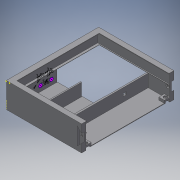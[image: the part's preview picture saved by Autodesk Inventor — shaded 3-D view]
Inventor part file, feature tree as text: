
AUTODESK INVENTOR PART (.ipt)
format: ipt  version: 2016 SP2 (Build 200236200, 236)  size: 1,028,608 bytes
history: native  units: mm
features: sketch x29, extrude x23, chamfer x14, projected_geometry x10, thread x2, revolve x2, other x2
ambient origin geometry x8: Origin, YZ Plane, XZ Plane, XY Plane, X Axis, Y Axis, Z Axis, Center Point
bodies: Volumenkörper1 (feature_tree), Volumenkörper4 (feature_tree), Volumenkörper5 (feature_tree)
feature tree (82):
  extrude  "Extrusion1"  Depth=9.0mm
  extrude  "Extrusion2"  Depth=10.0mm
  extrude  "Extrusion3"  Depth=1.0mm TaperAngle=0.0deg
  extrude  "Extrusion4"  Depth=1.5mm
  extrude  "Extrusion5"  Depth=17.0mm TaperAngle=0.0deg
  sketch  "Skizze6"  dims[d16=3.0mm d17=0.0mm d24=43.5mm]
  chamfer  "Fase2"  Distance=2.0mm
  chamfer  "Fase3"  Distance=23.0mm
  extrude  "Extrusion7"  Depth=43.5mm
  extrude  "Extrusion8"  Depth=2.0mm
  extrude  "Extrusion9"  Depth=1.5mm TaperAngle=45.0deg
  extrude  "Extrusion10"  Depth=78.5mm TaperAngle=0.0deg
  extrude  "Extrusion11"  Depth=82.5mm TaperAngle=0.0deg
  extrude  "Extrusion12"  Depth=2.0mm
  extrude  "Extrusion13"  Depth=1.0mm
  extrude  "Extrusion14"  Depth=2.0mm
  chamfer  "Fase4"  Distance=89.5mm
  chamfer  "Fase5"  Distance=4.5mm
  chamfer  "Fase6"  Distance=4.5mm
  chamfer  "Fase7"  Distance=2.0mm
  chamfer  "Fase9"  Distance=2.0mm
  chamfer  "Fase20"  Distance=2.0mm
  extrude  "Extrusion15"  Depth=2.0mm
  extrude  "Extrusion16"  Depth=5.0mm
  extrude  "Extrusion17"  Depth=5.0mm
  extrude  "Extrusion18"  Depth=40.0mm TaperAngle=0.0deg
  chamfer  "Fase14"  Distance=4.5mm
  chamfer  "Fase15"  Distance=18.0mm
  chamfer  "Fase16"  Distance=2.0mm
  chamfer  "Fase17"  Distance=2.0mm
  chamfer  "Fase18"  Distance=2.0mm
  chamfer  "Fase19"  Distance=2.0mm
  extrude  "Extrusion20"  Depth=10.0mm
  extrude  "Extrusion21"  Depth=10.0mm
  extrude  "Extrusion22"  Depth=10.0mm
  extrude  "Extrusion23"  Depth=10.0mm
  extrude  "Extrusion24"  Depth=10.0mm TaperAngle=0.0deg
  sketch  "Skizze26"  dims[d66=3.5mm d67=4.5mm d68=0.0mm]
  sketch  "Skizze27"  dims[d69=5.6mm d70=2.0mm d71=0.0mm d72=2.0mm d73=2.0mm d74=0.872665mm d75=2.0mm d76=2.0mm d77=0.872665mm]
  extrude  "Extrusion27"  Depth=10.0mm
  thread  "Gewinde3"  [1 undecoded]
  thread  "Gewinde4"  [1 undecoded]
  revolve  "Umdrehung3"
  other  "Spirale3"
  revolve  "Umdrehung4"
  other  "Spirale4"
  sketch  "Skizze1"  dims[d0=9.0mm d1=9.0mm]
  sketch  "Skizze2"  dims[d2=150.5mm d3=10.0mm]
  sketch  "Skizze3"  dims[d4=137.4mm d5=1.0mm d6=0.0mm]
  projected_geometry  "Projizierte Kontur1"
  sketch  "Skizze4"  dims[d7=1.5mm d8=1.5mm]
  projected_geometry  "Projizierte Kontur2"
  projected_geometry  "Projizierte Kontur3"
  projected_geometry  "Projizierte Kontur4"
  sketch  "Skizze5"  dims[d9=4.0mm d10=17.0mm d11=0.0mm d12=2.0mm d13=0.0mm d14=23.0mm d15=0.0mm]
  sketch  "Skizze7"  dims[d25=43.5mm d26=2.0mm]
  sketch  "Skizze8"  dims[d27=3.0mm d33=1.5mm d34=2.0mm d35=45.0deg]
  sketch  "Skizze9"  dims[d36=1.5mm d37=2.0mm d38=45.0deg d39=78.5mm d40=0.0mm]
  sketch  "Skizze10"  dims[d42=23.0mm d43=0.0mm d44=82.5mm d45=0.0mm]
  sketch  "Skizze11"  dims[d46=2.5mm d47=2.0mm]
  sketch  "Skizze13"  dims[d48=1.0mm d49=1.0mm]
  projected_geometry  "Projizierte Kontur5"
  sketch  "Skizze14"  dims[d50=89.5mm d51=0.0mm d52=2.0mm]
  sketch  "Skizze15"  dims[d53=1.0mm]
  sketch  "Skizze16"  dims[d54=2.0mm]
  projected_geometry  "Projizierte Kontur6"
  sketch  "Skizze17"  dims[d55=1.0mm d56=89.5mm d57=0.0mm]
  projected_geometry  "Projizierte Kontur7"
  sketch  "Skizze19"  dims[d58=15.0mm]
  projected_geometry  "Projizierte Kontur8"
  sketch  "Skizze21"  dims[d59=15.0mm]
  sketch  "Skizze22"  dims[d60=8.0mm]
  sketch  "Skizze23"  dims[d61=8.0mm]
  sketch  "Skizze24"  dims[d62=8.0mm]
  projected_geometry  "Projizierte Kontur9"
  projected_geometry  "Projizierte Kontur10"
  sketch  "Skizze25"  dims[d63=16.0mm d64=4.5mm d65=0.0mm]
  sketch  "Skizze28"  dims[d78=2.0mm d79=2.0mm d80=0.872665mm d81=2.0mm d82=2.0mm d83=0.872665mm]
  sketch  "Skizze33"  dims[d87=2.0mm d88=2.0mm d89=0.872665mm d90=5.0mm]
  sketch  "Skizze34"  dims[d91=5.0mm d92=40.0mm]
  sketch  "Skizze35"  dims[d93=9.0mm d94=40.0mm d95=0.0mm d96=4.5mm d97=0.0mm d98=18.0mm d99=0.0mm d100=2.0mm d101=0.0mm d114=2.0mm d115=2.0mm d116=0.872665mm d117=2.0mm d118=2.0mm d119=0.872665mm d120=2.0mm d121=2.0mm d122=0.872665mm]
  sketch  "Skizze36"  dims[d123=2.0mm d124=2.0mm d125=0.872665mm d126=2.0mm d127=2.0mm d128=0.872665mm d129=2.0mm d130=2.0mm d131=0.872665mm d134=2.0mm d135=2.0mm d136=0.872665mm d137=8.0mm d138=2.0mm d139=0.0mm d140=10.0mm d141=10.0mm d142=10.0mm d143=10.0mm d144=5.0mm d145=0.0mm d146=8.0mm d147=8.0mm d148=8.0mm d149=8.0mm d150=2.5mm d151=0.0mm d152=3.5mm d153=3.5mm d154=4.5mm d155=0.0mm d156=5.8mm d157=5.8mm d158=2.5mm d159=0.0mm d160=3.5mm d161=3.5mm d162=10.0mm d163=20.0mm d166=5.8mm d167=5.8mm d170=10.0mm d171=10.0mm d172=10.0mm d173=25.0mm d174=5.0mm d175=0.0mm d187=60.0deg d205=60.0deg d216=10.0mm d217=0.0mm d218=10.0mm d219=0.0mm d220=60.0deg d221=0.240125mm d222=0.240125mm d225=1.5mm d227=60.0deg d229=0.0mm d230=1.5015mm d231=8.0mm d232=10.0mm d233=0.0mm d234=0.0mm d235=0.0mm d236=0.0mm d237=0.0mm d238=60.0deg d239=0.240125mm d240=0.240125mm d243=1.5mm d245=60.0deg d247=0.0mm d248=1.5015mm d249=8.0mm d250=10.0mm d251=0.0mm d252=0.0mm d253=0.0mm d254=0.0mm d255=0.0mm]
note: 2 required parameter values undecoded (feature->parameter linkage not recoverable at this tier; creation-order binding heuristic only, values carry confidence <= 0.55)
